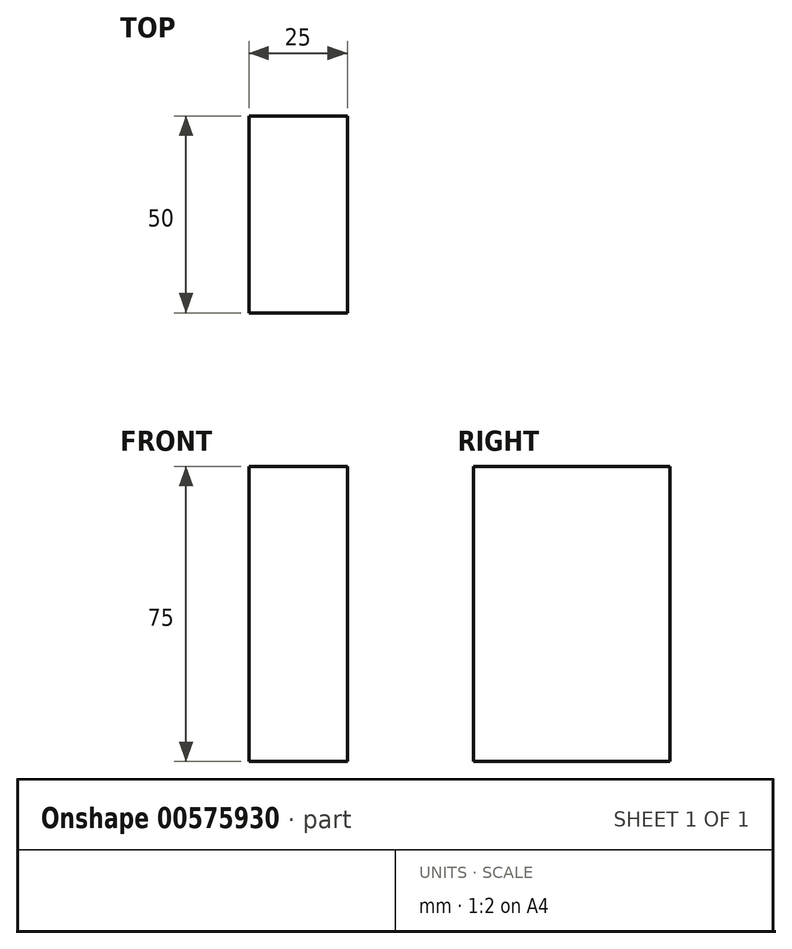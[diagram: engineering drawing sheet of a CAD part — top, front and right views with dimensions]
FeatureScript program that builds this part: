
annotation { "Feature Type Name" : "Feature", "Feature Type Description" : "" }
export const myFeature = defineFeature(function(context is Context, id is Id, definition is map)
    precondition{}
    {
        {
            var Q0;
            Q0=qCreatedBy(makeId("Top.planeOp"),FACE);
            var sketch = newSketch(context, id + "F0", { "sketchPlane" : qUnion([Q0])});
            skLineSegment(sketch, "E0.bottom", {"start": v(0, 0) * mm, "end": v(25, 0) * mm});
            skLineSegment(sketch, "E0.top", {"start": v(0, -50) * mm, "end": v(25, -50) * mm});
            skLineSegment(sketch, "E0.left", {"start": v(0, 0) * mm, "end": v(0, -50) * mm});
            skLineSegment(sketch, "E0.right", {"start": v(25, 0) * mm, "end": v(25, -50) * mm});
            skSolve(sketch);
        }
        {
            var Q0;
            Q0=makeQuery(id+"F0.imprint","IMPRINT",FACE,{"disambiguationData":[TD([[makeQuery(id+"F0.imprint","IMPRINT",EDGE,{"derivedFrom":sQuery(id+"F0.wireOp",EDGE,"E0.bottom")}),-1.0]])]});
            extrude(context, id + "F1", {"entities" : qUnion([Q0]), "depth" : 75 * mm, "offsetDistance" : 25 * mm});
        }
    });
